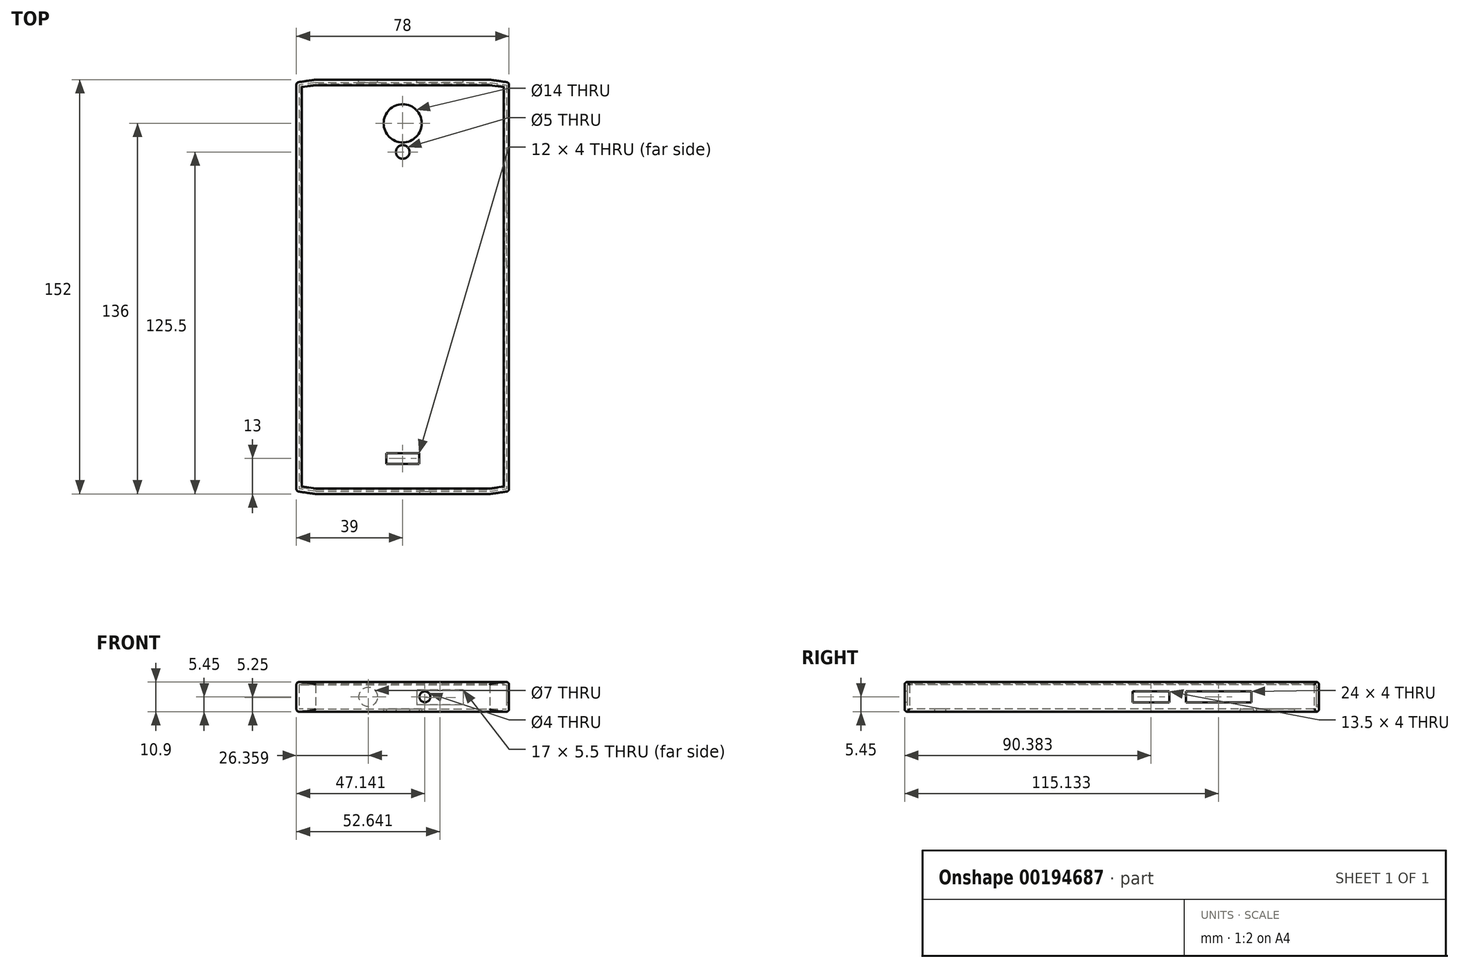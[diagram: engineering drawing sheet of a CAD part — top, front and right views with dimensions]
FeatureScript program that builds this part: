
annotation { "Feature Type Name" : "Feature", "Feature Type Description" : "" }
export const myFeature = defineFeature(function(context is Context, id is Id, definition is map)
    precondition{}
    {
        {
            var Q0;
            Q0=qCreatedBy(makeId("Top.planeOp"),FACE);
            var sketch = newSketch(context, id + "F0", { "sketchPlane" : qUnion([Q0])});
            skLineSegment(sketch, "E0.bottom", {"start": v(-32, 76) * mm, "end": v(32, 76) * mm});
            skLineSegment(sketch, "E0.top", {"start": v(-32, -76) * mm, "end": v(32, -76) * mm});
            skLineSegment(sketch, "E0.left", {"start": v(-39, 75) * mm, "end": v(-39, -75) * mm});
            skLineSegment(sketch, "E0.right", {"start": v(39, 75) * mm, "end": v(39, -75) * mm});
            skPoint(sketch, "E0.middle", {"position": v(0, 0) * mm});
            skCircle(sketch, "E1", {"center": v(0, 60) * mm, "radius": 7 * mm});
            skPoint(sketch, "E1.centerSnap0", {"position": v(0, 76) * mm});
            skCircle(sketch, "E2", {"center": v(0, 49.5) * mm, "radius": 2.5 * mm});
            skLineSegment(sketch, "E3.bottom", {"start": v(-6, -61) * mm, "end": v(6, -61) * mm});
            skLineSegment(sketch, "E3.top", {"start": v(-6, -65) * mm, "end": v(6, -65) * mm});
            skLineSegment(sketch, "E3.left", {"start": v(-6, -61) * mm, "end": v(-6, -65) * mm});
            skLineSegment(sketch, "E3.right", {"start": v(6, -61) * mm, "end": v(6, -65) * mm});
            skPoint(sketch, "E3.middle", {"position": v(0, -63) * mm});
            skLineSegment(sketch, "E4", {"start": v(32, 76) * mm, "end": v(39, 75) * mm});
            skPoint(sketch, "E5.orphan", {"position": v(39, 76) * mm});
            skLineSegment(sketch, "E6.MirrorCS", {"start": v(-32, 76) * mm, "end": v(-39, 75) * mm});
            skPoint(sketch, "E7.orphan", {"position": v(-39, 76) * mm});
            skLineSegment(sketch, "E8.MirrorCS", {"start": v(-32, -76) * mm, "end": v(-39, -75) * mm});
            skLineSegment(sketch, "E9.MirrorCS", {"start": v(32, -76) * mm, "end": v(39, -75) * mm});
            skPoint(sketch, "E10.orphan", {"position": v(-39, -76) * mm});
            skPoint(sketch, "E11.orphan", {"position": v(39, -76) * mm});
            skSolve(sketch);
        }
        {
            var Q0;
            Q0=makeQuery(id+"F0.imprint","IMPRINT",FACE,{"disambiguationData":[TD([[makeQuery(id+"F0.imprint","IMPRINT",EDGE,{"derivedFrom":sQuery(id+"F0.wireOp",EDGE,"E0.bottom")}),-1.0]])]});
            extrude(context, id + "F1", {"entities" : qUnion([Q0]), "depth" : 1 * mm});
        }
        {
            var Q0;
            Q0=makeQuery(id+"F1.opExtrude","CAP_FACE",FACE,{"disambiguationData":[OSD([sQuery(id+"F0.wireOp",EDGE,"E0.bottom"),sQuery(id+"F0.wireOp",EDGE,"E0.top"),sQuery(id+"F0.wireOp",EDGE,"E0.left"),sQuery(id+"F0.wireOp",EDGE,"E0.right")])],"isStart":false});
            var sketch = newSketch(context, id + "F2", { "sketchPlane" : qUnion([Q0])});
            skLineSegment(sketch, "E12.0", {"start": v(-31.93, -75) * mm, "end": v(-38, -74.13) * mm});
            skLineSegment(sketch, "E12.1", {"start": v(-38, 74.13) * mm, "end": v(-38, -74.13) * mm});
            skLineSegment(sketch, "E12.2", {"start": v(-31.93, -75) * mm, "end": v(31.93, -75) * mm});
            skLineSegment(sketch, "E12.3", {"start": v(-31.93, 75) * mm, "end": v(-38, 74.13) * mm});
            skLineSegment(sketch, "E12.4", {"start": v(31.93, -75) * mm, "end": v(38, -74.13) * mm});
            skLineSegment(sketch, "E12.5", {"start": v(38, 74.13) * mm, "end": v(38, -74.13) * mm});
            skLineSegment(sketch, "E12.6", {"start": v(31.93, 75) * mm, "end": v(38, 74.13) * mm});
            skLineSegment(sketch, "E12.7", {"start": v(-31.93, 75) * mm, "end": v(31.93, 75) * mm});
            skSolve(sketch);
        }
        {
            var Q0;
            Q0=makeQuery(id+"F2.imprint","IMPRINT",FACE,{"disambiguationData":[TD([[makeQuery(id+"F2.imprint","IMPRINT",EDGE,{"derivedFrom":sQuery(id+"F2.wireOp",EDGE,"E12.0")}),1.0]])]});
            extrude(context, id + "F3", {"entities" : qUnion([Q0]), "operationType" : NewBodyOperationType.ADD, "depth" : 8.9 * mm});
        }
        {
            var Q0;
            Q0=makeQuery(id+"F3.opExtrude","CAP_FACE",FACE,{"disambiguationData":[OSD([sQuery(id+"F0.wireOp",EDGE,"E0.bottom"),sQuery(id+"F0.wireOp",EDGE,"E0.top"),sQuery(id+"F0.wireOp",EDGE,"E0.left"),sQuery(id+"F0.wireOp",EDGE,"E0.right"),sQuery(id+"F2.wireOp",EDGE,"e6dc9c99-4e71-4461-9361-1a2e7a1af92a.0"),sQuery(id+"F2.wireOp",EDGE,"e6dc9c99-4e71-4461-9361-1a2e7a1af92a.1"),sQuery(id+"F2.wireOp",EDGE,"e6dc9c99-4e71-4461-9361-1a2e7a1af92a.2"),sQuery(id+"F2.wireOp",EDGE,"e6dc9c99-4e71-4461-9361-1a2e7a1af92a.3")])],"isStart":false});
            var sketch = newSketch(context, id + "F4", { "sketchPlane" : qUnion([Q0])});
            skLineSegment(sketch, "E13.0", {"start": v(-31.86, 74) * mm, "end": v(-37, 73.27) * mm});
            skLineSegment(sketch, "E13.1", {"start": v(-37, 73.27) * mm, "end": v(-37, -73.27) * mm});
            skLineSegment(sketch, "E13.2", {"start": v(-31.86, 74) * mm, "end": v(31.86, 74) * mm});
            skLineSegment(sketch, "E13.3", {"start": v(-31.86, -74) * mm, "end": v(-37, -73.27) * mm});
            skLineSegment(sketch, "E13.4", {"start": v(31.86, 74) * mm, "end": v(37, 73.27) * mm});
            skLineSegment(sketch, "E13.5", {"start": v(37, 73.27) * mm, "end": v(37, -73.27) * mm});
            skLineSegment(sketch, "E13.6", {"start": v(31.86, -74) * mm, "end": v(37, -73.27) * mm});
            skLineSegment(sketch, "E13.7", {"start": v(-31.86, -74) * mm, "end": v(31.86, -74) * mm});
            skSolve(sketch);
        }
        {
            var Q0;
            Q0=makeQuery(id+"F4.imprint","IMPRINT",FACE,{"disambiguationData":[TD([[makeQuery(id+"F4.imprint","IMPRINT",EDGE,{"derivedFrom":makeQuery(id+"F3.opExtrude","CAP_EDGE",EDGE,{"disambiguationData":[OSD([sQuery(id+"F2.wireOp",EDGE,"E12.0")])],"isStart":false})}),1.0]])]});
            var Q1;
            Q1=makeQuery(id+"F4.imprint","IMPRINT",FACE,{"disambiguationData":[TD([[makeQuery(id+"F4.imprint","IMPRINT",EDGE,{"derivedFrom":sQuery(id+"F4.wireOp",EDGE,"E13.0")}),-1.0]])]});
            extrude(context, id + "F5", {"entities" : qUnion([Q0, Q1]), "operationType" : NewBodyOperationType.ADD, "depth" : 1 * mm});
        }
        {
            var Q0;
            Q0=makeQuery(id+"F5.opExtrude","CAP_EDGE",EDGE,{"disambiguationData":[OSD([sQuery(id+"F0.wireOp",EDGE,"E0.left")])],"isStart":false});
            var Q1;
            Q1=makeQuery(id+"F5.opExtrude","CAP_EDGE",EDGE,{"disambiguationData":[OSD([sQuery(id+"F0.wireOp",EDGE,"E0.bottom")])],"isStart":false});
            var Q2;
            Q2=makeQuery(id+"F5.opExtrude","CAP_EDGE",EDGE,{"disambiguationData":[OSD([sQuery(id+"F0.wireOp",EDGE,"E0.top")])],"isStart":false});
            var Q3;
            Q3=makeQuery(id+"F5.opExtrude","CAP_EDGE",EDGE,{"disambiguationData":[OSD([sQuery(id+"F0.wireOp",EDGE,"E0.right")])],"isStart":false});
            var Q4;
            {var subQ0=sQuery(id+"F0.wireOp",EDGE,"E0.right");var subQ1=sQuery(id+"F0.wireOp",EDGE,"E0.top");Q4=makeQuery(id+"F5.boolean.opBoolean","MERGE",EDGE,{"derivedFrom":[makeQuery(id+"F3.boolean.opBoolean","MERGE",EDGE,{"derivedFrom":[makeQuery(id+"F1.opExtrude","SWEPT_EDGE",EDGE,{"disambiguationData":[OSD([subQ1,subQ0])]}),makeQuery(id+"F3.opExtrude","SWEPT_EDGE",EDGE,{"disambiguationData":[OSD([subQ1,subQ0])]})]}),makeQuery(id+"F5.opExtrude","SWEPT_EDGE",EDGE,{"disambiguationData":[OSD([subQ1,subQ0])]})]});}
            var Q5;
            Q5=makeQuery(id+"F1.opExtrude","CAP_EDGE",EDGE,{"disambiguationData":[OSD([sQuery(id+"F0.wireOp",EDGE,"E0.top")])],"isStart":true});
            var Q6;
            Q6=makeQuery(id+"F1.opExtrude","CAP_EDGE",EDGE,{"disambiguationData":[OSD([sQuery(id+"F0.wireOp",EDGE,"E0.right")])],"isStart":true});
            var Q7;
            {var subQ0=sQuery(id+"F0.wireOp",EDGE,"E0.left");var subQ1=sQuery(id+"F0.wireOp",EDGE,"E0.top");Q7=makeQuery(id+"F5.boolean.opBoolean","MERGE",EDGE,{"derivedFrom":[makeQuery(id+"F3.boolean.opBoolean","MERGE",EDGE,{"derivedFrom":[makeQuery(id+"F1.opExtrude","SWEPT_EDGE",EDGE,{"disambiguationData":[OSD([subQ1,subQ0])]}),makeQuery(id+"F3.opExtrude","SWEPT_EDGE",EDGE,{"disambiguationData":[OSD([subQ1,subQ0])]})]}),makeQuery(id+"F5.opExtrude","SWEPT_EDGE",EDGE,{"disambiguationData":[OSD([subQ1,subQ0])]})]});}
            var Q8;
            Q8=makeQuery(id+"F1.opExtrude","CAP_EDGE",EDGE,{"disambiguationData":[OSD([sQuery(id+"F0.wireOp",EDGE,"E0.left")])],"isStart":true});
            var Q9;
            {var subQ0=sQuery(id+"F0.wireOp",EDGE,"E0.left");var subQ1=sQuery(id+"F0.wireOp",EDGE,"E0.bottom");Q9=makeQuery(id+"F5.boolean.opBoolean","MERGE",EDGE,{"derivedFrom":[makeQuery(id+"F3.boolean.opBoolean","MERGE",EDGE,{"derivedFrom":[makeQuery(id+"F1.opExtrude","SWEPT_EDGE",EDGE,{"disambiguationData":[OSD([subQ1,subQ0])]}),makeQuery(id+"F3.opExtrude","SWEPT_EDGE",EDGE,{"disambiguationData":[OSD([subQ1,subQ0])]})]}),makeQuery(id+"F5.opExtrude","SWEPT_EDGE",EDGE,{"disambiguationData":[OSD([subQ1,subQ0])]})]});}
            var Q10;
            {var subQ0=sQuery(id+"F0.wireOp",EDGE,"E0.right");var subQ1=sQuery(id+"F0.wireOp",EDGE,"E0.bottom");Q10=makeQuery(id+"F5.boolean.opBoolean","MERGE",EDGE,{"derivedFrom":[makeQuery(id+"F3.boolean.opBoolean","MERGE",EDGE,{"derivedFrom":[makeQuery(id+"F1.opExtrude","SWEPT_EDGE",EDGE,{"disambiguationData":[OSD([subQ1,subQ0])]}),makeQuery(id+"F3.opExtrude","SWEPT_EDGE",EDGE,{"disambiguationData":[OSD([subQ1,subQ0])]})]}),makeQuery(id+"F5.opExtrude","SWEPT_EDGE",EDGE,{"disambiguationData":[OSD([subQ1,subQ0])]})]});}
            var Q11;
            Q11=makeQuery(id+"F1.opExtrude","CAP_EDGE",EDGE,{"disambiguationData":[OSD([sQuery(id+"F0.wireOp",EDGE,"E0.bottom")])],"isStart":true});
            var Q12;
            Q12=makeQuery(id+"F5.opExtrude","CAP_EDGE",EDGE,{"disambiguationData":[OSD([sQuery(id+"F4.wireOp",EDGE,"7eff3cd0-2243-4cc3-8ade-aa6051ac1e62.3")])],"isStart":false});
            var Q13;
            Q13=makeQuery(id+"F5.opExtrude","CAP_EDGE",EDGE,{"disambiguationData":[OSD([sQuery(id+"F4.wireOp",EDGE,"7eff3cd0-2243-4cc3-8ade-aa6051ac1e62.0")])],"isStart":false});
            var Q14;
            Q14=makeQuery(id+"F5.opExtrude","CAP_EDGE",EDGE,{"disambiguationData":[OSD([sQuery(id+"F4.wireOp",EDGE,"7eff3cd0-2243-4cc3-8ade-aa6051ac1e62.1")])],"isStart":false});
            var Q15;
            Q15=makeQuery(id+"F5.opExtrude","CAP_EDGE",EDGE,{"disambiguationData":[OSD([sQuery(id+"F4.wireOp",EDGE,"7eff3cd0-2243-4cc3-8ade-aa6051ac1e62.2")])],"isStart":false});
            fillet(context, id + "F6", {"entities" : qUnion([Q0, Q1, Q2, Q3, Q4, Q5, Q6, Q7, Q8, Q9, Q10, Q11, Q12, Q13, Q14, Q15]), "radius" : 1 * mm, "tangentPropagation" : true, "allowEdgeOverflow" : false});
        }
        {
            var Q0;
            Q0=makeQuery(id+"F5.opExtrude","CAP_EDGE",EDGE,{"disambiguationData":[OSD([sQuery(id+"F4.wireOp",EDGE,"E13.0")])],"isStart":true});
            var Q1;
            Q1=makeQuery(id+"F5.opExtrude","CAP_EDGE",EDGE,{"disambiguationData":[OSD([sQuery(id+"F4.wireOp",EDGE,"E13.1")])],"isStart":true});
            var Q2;
            Q2=makeQuery(id+"F5.opExtrude","CAP_EDGE",EDGE,{"disambiguationData":[OSD([sQuery(id+"F4.wireOp",EDGE,"E13.2")])],"isStart":true});
            var Q3;
            Q3=makeQuery(id+"F5.opExtrude","CAP_EDGE",EDGE,{"disambiguationData":[OSD([sQuery(id+"F4.wireOp",EDGE,"E13.4")])],"isStart":true});
            var Q4;
            Q4=makeQuery(id+"F5.opExtrude","CAP_EDGE",EDGE,{"disambiguationData":[OSD([sQuery(id+"F4.wireOp",EDGE,"E13.5")])],"isStart":true});
            var Q5;
            Q5=makeQuery(id+"F5.opExtrude","CAP_EDGE",EDGE,{"disambiguationData":[OSD([sQuery(id+"F4.wireOp",EDGE,"E13.6")])],"isStart":true});
            var Q6;
            Q6=makeQuery(id+"F5.opExtrude","CAP_EDGE",EDGE,{"disambiguationData":[OSD([sQuery(id+"F4.wireOp",EDGE,"E13.7")])],"isStart":true});
            var Q7;
            Q7=makeQuery(id+"F5.opExtrude","CAP_EDGE",EDGE,{"disambiguationData":[OSD([sQuery(id+"F4.wireOp",EDGE,"E13.3")])],"isStart":true});
            chamfer(context, id + "F7", {"entities" : qUnion([Q0, Q1, Q2, Q3, Q4, Q5, Q6, Q7]), "width" : 0.4 * mm, "tangentPropagation" : true});
        }
        {
            var Q0;
            {var subQ0=sQuery(id+"F0.wireOp",EDGE,"E0.right");Q0=makeQuery(id+"F5.boolean.opBoolean","MERGE",FACE,{"derivedFrom":[makeQuery(id+"F3.boolean.opBoolean","MERGE",FACE,{"derivedFrom":[makeQuery(id+"F1.opExtrude","SWEPT_FACE",FACE,{"disambiguationData":[OSD([subQ0])]}),makeQuery(id+"F3.opExtrude","SWEPT_FACE",FACE,{"disambiguationData":[OSD([subQ0])]})]}),makeQuery(id+"F5.opExtrude","SWEPT_FACE",FACE,{"disambiguationData":[OSD([subQ0])]})]});}
            var sketch = newSketch(context, id + "F8", { "sketchPlane" : qUnion([Q0])});
            skLineSegment(sketch, "E14.bottom", {"start": v(27.13, 7.45) * mm, "end": v(51.13, 7.45) * mm});
            skLineSegment(sketch, "E14.top", {"start": v(27.13, 3.45) * mm, "end": v(51.13, 3.45) * mm});
            skLineSegment(sketch, "E14.left", {"start": v(27.13, 7.45) * mm, "end": v(27.13, 3.45) * mm});
            skLineSegment(sketch, "E14.right", {"start": v(51.13, 7.45) * mm, "end": v(51.13, 3.45) * mm});
            skPoint(sketch, "E14.middle", {"position": v(39.13, 5.45) * mm});
            skLineSegment(sketch, "E15", {"start": v(39.13, 9.9) * mm, "end": v(39.13, 1) * mm, "construction": true});
            skPoint(sketch, "E15.startSnap0", {"position": v(39.13, 7.45) * mm});
            skPoint(sketch, "E15.endSnap0", {"position": v(39.13, 3.45) * mm});
            skLineSegment(sketch, "E16.bottom", {"start": v(7.63, 7.45) * mm, "end": v(21.13, 7.45) * mm});
            skLineSegment(sketch, "E16.top", {"start": v(7.63, 3.45) * mm, "end": v(21.13, 3.45) * mm});
            skLineSegment(sketch, "E16.left", {"start": v(7.63, 7.45) * mm, "end": v(7.63, 3.45) * mm});
            skLineSegment(sketch, "E16.right", {"start": v(21.13, 7.45) * mm, "end": v(21.13, 3.45) * mm});
            skPoint(sketch, "E16.middle", {"position": v(14.38, 5.45) * mm});
            skSolve(sketch);
        }
        {
            var Q0;
            Q0=makeQuery(id+"F8.imprint","IMPRINT",FACE,{"disambiguationData":[TD([[makeQuery(id+"F8.imprint","IMPRINT",EDGE,{"derivedFrom":sQuery(id+"F8.wireOp",EDGE,"E16.bottom")}),-1.0]])]});
            var Q1;
            Q1=makeQuery(id+"F8.imprint","IMPRINT",FACE,{"disambiguationData":[TD([[makeQuery(id+"F8.imprint","IMPRINT",EDGE,{"derivedFrom":sQuery(id+"F8.wireOp",EDGE,"E14.bottom")}),-1.0]])]});
            extrude(context, id + "F9", {"entities" : qUnion([Q0, Q1]), "operationType" : NewBodyOperationType.REMOVE, "oppositeDirection" : true, "depth" : 25 * mm});
        }
        {
            var Q0;
            {var subQ0=sQuery(id+"F0.wireOp",EDGE,"E0.bottom");Q0=makeQuery(id+"F5.boolean.opBoolean","MERGE",FACE,{"derivedFrom":[makeQuery(id+"F3.boolean.opBoolean","MERGE",FACE,{"derivedFrom":[makeQuery(id+"F1.opExtrude","SWEPT_FACE",FACE,{"disambiguationData":[OSD([subQ0])]}),makeQuery(id+"F3.opExtrude","SWEPT_FACE",FACE,{"disambiguationData":[OSD([subQ0])]})]}),makeQuery(id+"F5.opExtrude","SWEPT_FACE",FACE,{"disambiguationData":[OSD([subQ0])]})]});}
            var sketch = newSketch(context, id + "F10", { "sketchPlane" : qUnion([Q0])});
            skPoint(sketch, "E17.middle.positionSnap0", {"position": v(31.93, 5.45) * mm});
            skPoint(sketch, "E17.centerSnap0", {"position": v(31.93, 5.45) * mm});
            skLineSegment(sketch, "E18.bottom", {"start": v(-22.14, 8) * mm, "end": v(-5.14, 8) * mm});
            skLineSegment(sketch, "E18.top", {"start": v(-22.14, 2.5) * mm, "end": v(-5.14, 2.5) * mm});
            skLineSegment(sketch, "E18.right", {"start": v(-5.14, 8) * mm, "end": v(-5.14, 2.5) * mm});
            skPoint(sketch, "E18.middle", {"position": v(-13.64, 5.25) * mm});
            skCircle(sketch, "E19", {"center": v(12.64, 5.45) * mm, "radius": 3.5 * mm});
            skLineSegment(sketch, "E20", {"start": v(-22.14, 8) * mm, "end": v(-22.14, 2.5) * mm});
            skSolve(sketch);
        }
        {
            var Q0;
            Q0=makeQuery(id+"F10.imprint","IMPRINT",FACE,{"disambiguationData":[TD([[makeQuery(id+"F10.imprint","IMPRINT",EDGE,{"derivedFrom":sQuery(id+"F10.wireOp",EDGE,"E19")}),1.0]])]});
            var Q1;
            Q1=makeQuery(id+"F10.imprint","IMPRINT",FACE,{"disambiguationData":[TD([[makeQuery(id+"F10.imprint","IMPRINT",EDGE,{"derivedFrom":sQuery(id+"F10.wireOp",EDGE,"E18.bottom")}),-1.0]])]});
            extrude(context, id + "F11", {"entities" : qUnion([Q0, Q1]), "operationType" : NewBodyOperationType.REMOVE, "oppositeDirection" : true, "depth" : 25 * mm});
        }
        {
            var Q0;
            {var subQ0=sQuery(id+"F0.wireOp",EDGE,"E0.top");Q0=makeQuery(id+"F5.boolean.opBoolean","MERGE",FACE,{"derivedFrom":[makeQuery(id+"F3.boolean.opBoolean","MERGE",FACE,{"derivedFrom":[makeQuery(id+"F1.opExtrude","SWEPT_FACE",FACE,{"disambiguationData":[OSD([subQ0])]}),makeQuery(id+"F3.opExtrude","SWEPT_FACE",FACE,{"disambiguationData":[OSD([subQ0])]})]}),makeQuery(id+"F5.opExtrude","SWEPT_FACE",FACE,{"disambiguationData":[OSD([subQ0])]})]});}
            var sketch = newSketch(context, id + "F12", { "sketchPlane" : qUnion([Q0])});
            skCircle(sketch, "E21", {"center": v(8.14, 5.45) * mm, "radius": 2 * mm});
            skPoint(sketch, "E21.centerSnap0", {"position": v(-31.93, 5.45) * mm});
            skSolve(sketch);
        }
        {
            var Q0;
            Q0=makeQuery(id+"F12.imprint","IMPRINT",FACE,{"disambiguationData":[TD([[makeQuery(id+"F12.imprint","IMPRINT",EDGE,{"derivedFrom":sQuery(id+"F12.wireOp",EDGE,"E21")}),1.0]])]});
            var Q1;
            Q1=sQuery(id+"F12.wireOp",EDGE,"E21");
            extrude(context, id + "F13", {"entities" : qUnion([Q0]), "operationType" : NewBodyOperationType.REMOVE, "surfaceEntities" : qUnion([Q1]), "oppositeDirection" : true, "depth" : 25 * mm});
        }
    });
